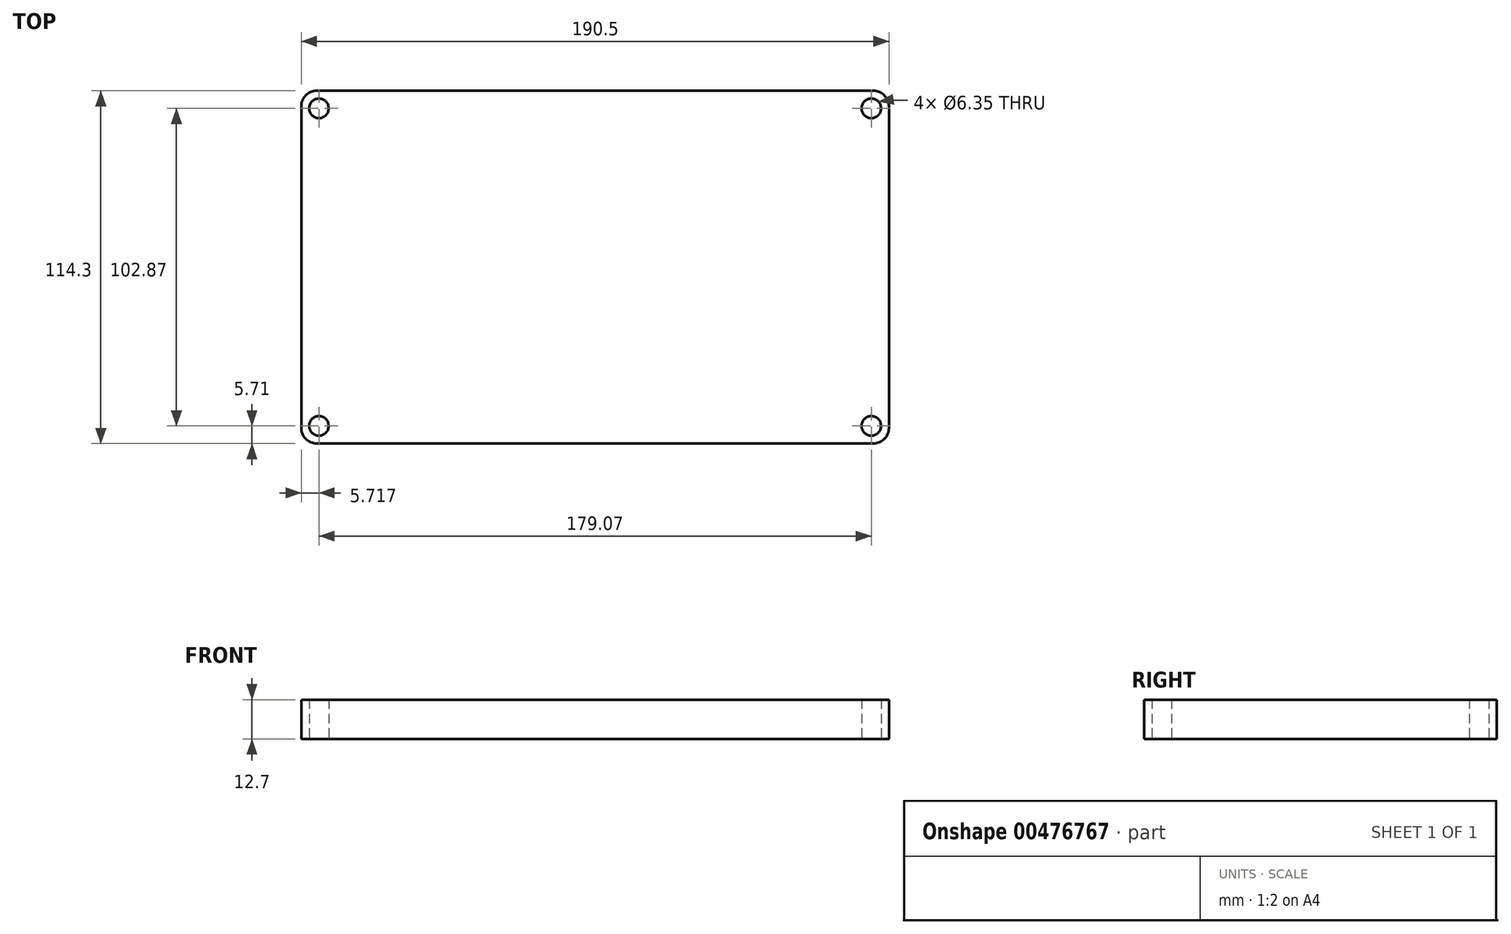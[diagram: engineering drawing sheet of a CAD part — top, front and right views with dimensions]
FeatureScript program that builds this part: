
annotation { "Feature Type Name" : "Feature", "Feature Type Description" : "" }
export const myFeature = defineFeature(function(context is Context, id is Id, definition is map)
    precondition{}
    {
        {
            var Q0;
            Q0=qCreatedBy(makeId("Top.planeOp"),FACE);
            var sketch = newSketch(context, id + "F0", { "sketchPlane" : qUnion([Q0])});
            skLineSegment(sketch, "E0.bottom", {"start": v(-96.69, 21.09) * mm, "end": v(93.81, 21.09) * mm});
            skLineSegment(sketch, "E0.top", {"start": v(-96.69, -93.21) * mm, "end": v(93.81, -93.21) * mm});
            skLineSegment(sketch, "E0.left", {"start": v(-96.69, 21.09) * mm, "end": v(-96.69, -93.21) * mm});
            skLineSegment(sketch, "E0.right", {"start": v(93.81, 21.09) * mm, "end": v(93.81, -93.21) * mm});
            skCircle(sketch, "E1.MirrorC", {"center": v(88.1, 15.37) * mm, "radius": 3.18 * mm});
            skPoint(sketch, "E2", {"position": v(88.1, 18.55) * mm});
            skPoint(sketch, "E3", {"position": v(91.27, 15.37) * mm});
            skPoint(sketch, "E4.endSnap0", {"position": v(93.81, -36.06) * mm});
            skPoint(sketch, "E5.endSnap0", {"position": v(-1.44, 21.09) * mm});
            skCircle(sketch, "E6.MirrorC", {"center": v(-90.97, 15.37) * mm, "radius": 3.18 * mm});
            skCircle(sketch, "E7.MirrorC", {"center": v(-90.97, -87.5) * mm, "radius": 3.18 * mm});
            skCircle(sketch, "E8.MirrorC", {"center": v(88.1, -87.5) * mm, "radius": 3.18 * mm});
            skSolve(sketch);
        }
        {
            var Q0;
            Q0=makeQuery(id+"F0.imprint","IMPRINT",FACE,{"disambiguationData":[TD([[makeQuery(id+"F0.imprint","IMPRINT",EDGE,{"derivedFrom":sQuery(id+"F0.wireOp",EDGE,"E0.bottom")}),-1.0]])]});
            extrude(context, id + "F1", {"entities" : qUnion([Q0]), "depth" : 12.7 * mm});
        }
        {
            var Q0;
            Q0=makeQuery(id+"F1.opExtrude","SWEPT_EDGE",EDGE,{"disambiguationData":[OSD([sQuery(id+"F0.wireOp",EDGE,"E0.top"),sQuery(id+"F0.wireOp",EDGE,"E0.right")])]});
            var Q1;
            Q1=makeQuery(id+"F1.opExtrude","SWEPT_EDGE",EDGE,{"disambiguationData":[OSD([sQuery(id+"F0.wireOp",EDGE,"E0.bottom"),sQuery(id+"F0.wireOp",EDGE,"E0.right")])]});
            var Q2;
            Q2=makeQuery(id+"F1.opExtrude","SWEPT_EDGE",EDGE,{"disambiguationData":[OSD([sQuery(id+"F0.wireOp",EDGE,"E0.bottom"),sQuery(id+"F0.wireOp",EDGE,"E0.left")])]});
            var Q3;
            Q3=makeQuery(id+"F1.opExtrude","SWEPT_EDGE",EDGE,{"disambiguationData":[OSD([sQuery(id+"F0.wireOp",EDGE,"E0.top"),sQuery(id+"F0.wireOp",EDGE,"E0.left")])]});
            fillet(context, id + "F2", {"entities" : qUnion([Q0, Q1, Q2, Q3]), "radius" : 5.08 * mm, "tangentPropagation" : true, "allowEdgeOverflow" : false});
        }
    });
